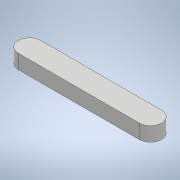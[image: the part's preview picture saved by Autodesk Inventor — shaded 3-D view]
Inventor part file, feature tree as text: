
AUTODESK INVENTOR PART (.ipt)
format: ipt  version: 2020 (Build 240168000, 168)  size: 100,352 bytes
history: native  units: mm
features: other x3, extrude x1, sketch x1, reference x1
ambient origin geometry x8: Origin, YZ Plane, XZ Plane, XY Plane, X Axis, Y Axis, Z Axis, Center Point
bodies: Body1 (feature_tree)
feature tree (6):
  extrude  "拉伸2"  Depth=7.0mm
  sketch  "草图1"  dims[d2=90.0mm d3=7.0mm d4=9.0mm d5=0.0mm d6=0.5mm d7=0.872665mm]
  reference  "参考1"
  other  "<userpath>\Desktop\111111\Workspace\cpz assemble.iam"
  other  "cpz assemble.iam"
  other  "轴:1"
